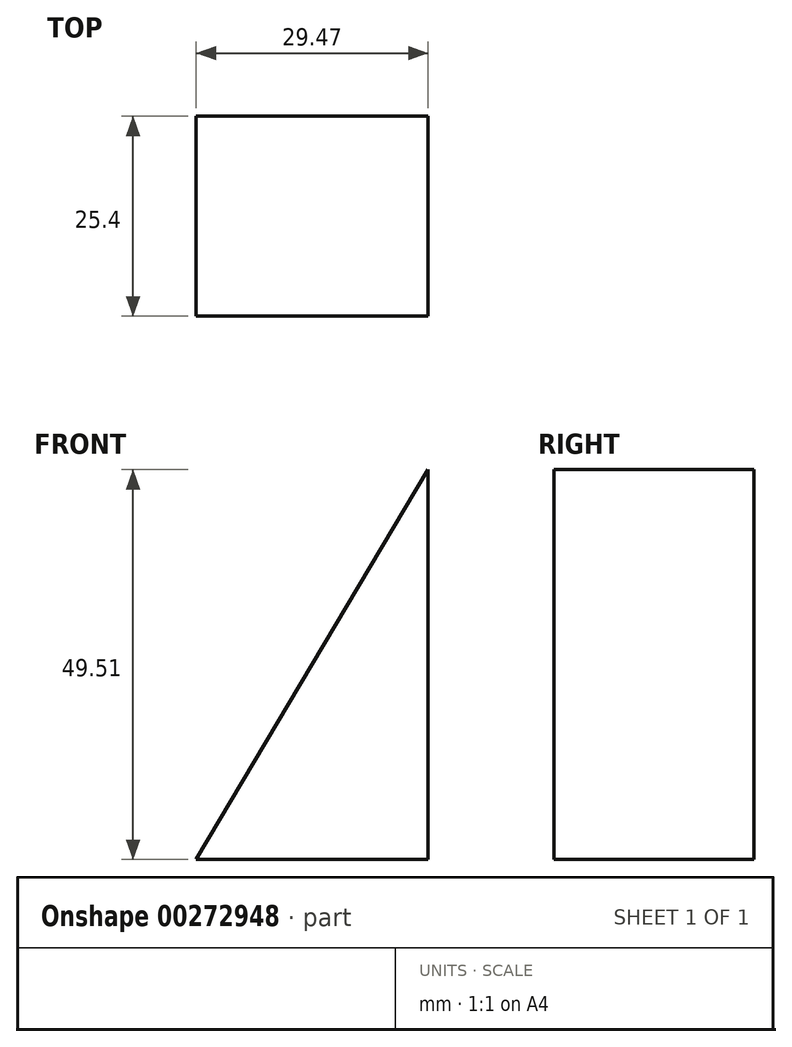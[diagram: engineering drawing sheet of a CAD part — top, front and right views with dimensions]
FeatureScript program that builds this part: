
annotation { "Feature Type Name" : "Feature", "Feature Type Description" : "" }
export const myFeature = defineFeature(function(context is Context, id is Id, definition is map)
    precondition{}
    {
        {
            var Q0;
            Q0=qCreatedBy(makeId("Front.planeOp"),FACE);
            var sketch = newSketch(context, id + "F0", { "sketchPlane" : qUnion([Q0])});
            skLineSegment(sketch, "E0", {"start": v(0, 0) * mm, "end": v(0, 49.51) * mm});
            skLineSegment(sketch, "E1", {"start": v(0, 49.51) * mm, "end": v(-29.47, 0) * mm});
            skLineSegment(sketch, "E2", {"start": v(-29.47, 0) * mm, "end": v(0, 0) * mm});
            skSolve(sketch);
        }
        {
            var Q0;
            Q0 = qSketchRegion(id + "F0", true);
            extrude(context, id + "F1", {"entities" : qUnion([Q0]), "depth" : 25.4 * mm});
        }
    });
